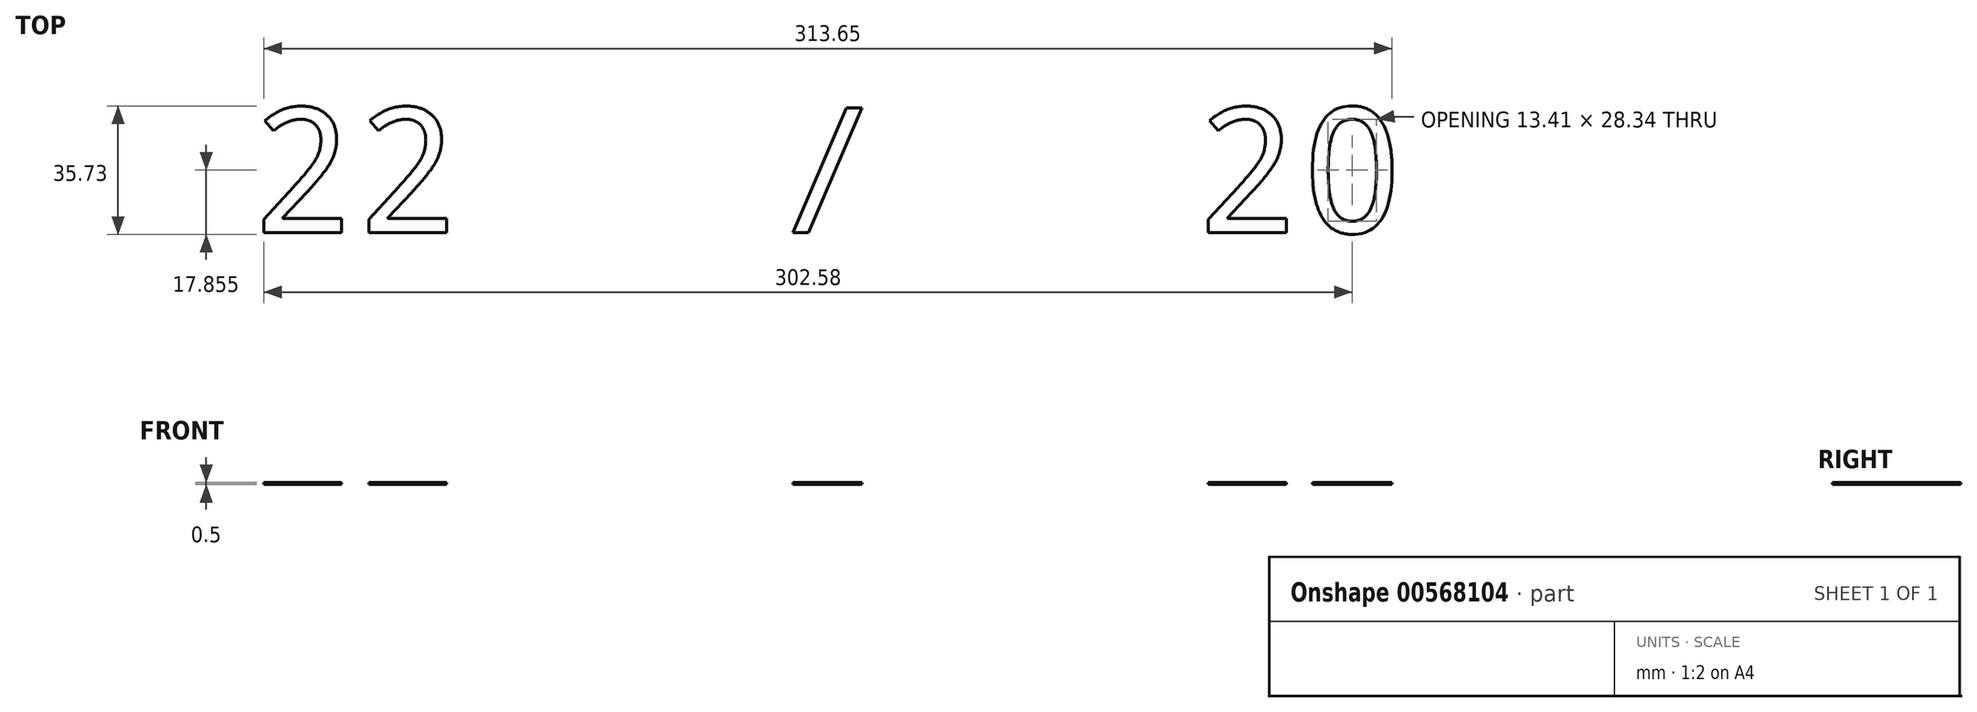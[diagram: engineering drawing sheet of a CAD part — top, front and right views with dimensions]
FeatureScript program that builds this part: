
annotation { "Feature Type Name" : "Feature", "Feature Type Description" : "" }
export const myFeature = defineFeature(function(context is Context, id is Id, definition is map)
    precondition{}
    {
        {
            var Q0;
            Q0=qCreatedBy(makeId("Top.planeOp"),FACE);
            var sketch = newSketch(context, id + "F0", { "sketchPlane" : qUnion([Q0])});
            skText(sketch, "E0", { "text": "22   /   20", "fontName": "DroidSansMono.ttf"});
            const initialGuessF0  = {"E0": [-0.1697, 0, 1, 0, 0.035]};
            skSetInitialGuess(sketch, initialGuessF0);
            skSolve(sketch);
        }
        {
            var Q0;
            Q0 = qSketchRegion(id + "F0", true);
            extrude(context, id + "F1", {"entities" : qUnion([Q0]), "depth" : 0.5 * mm, "offsetDistance" : 25.4 * mm});
        }
    });
